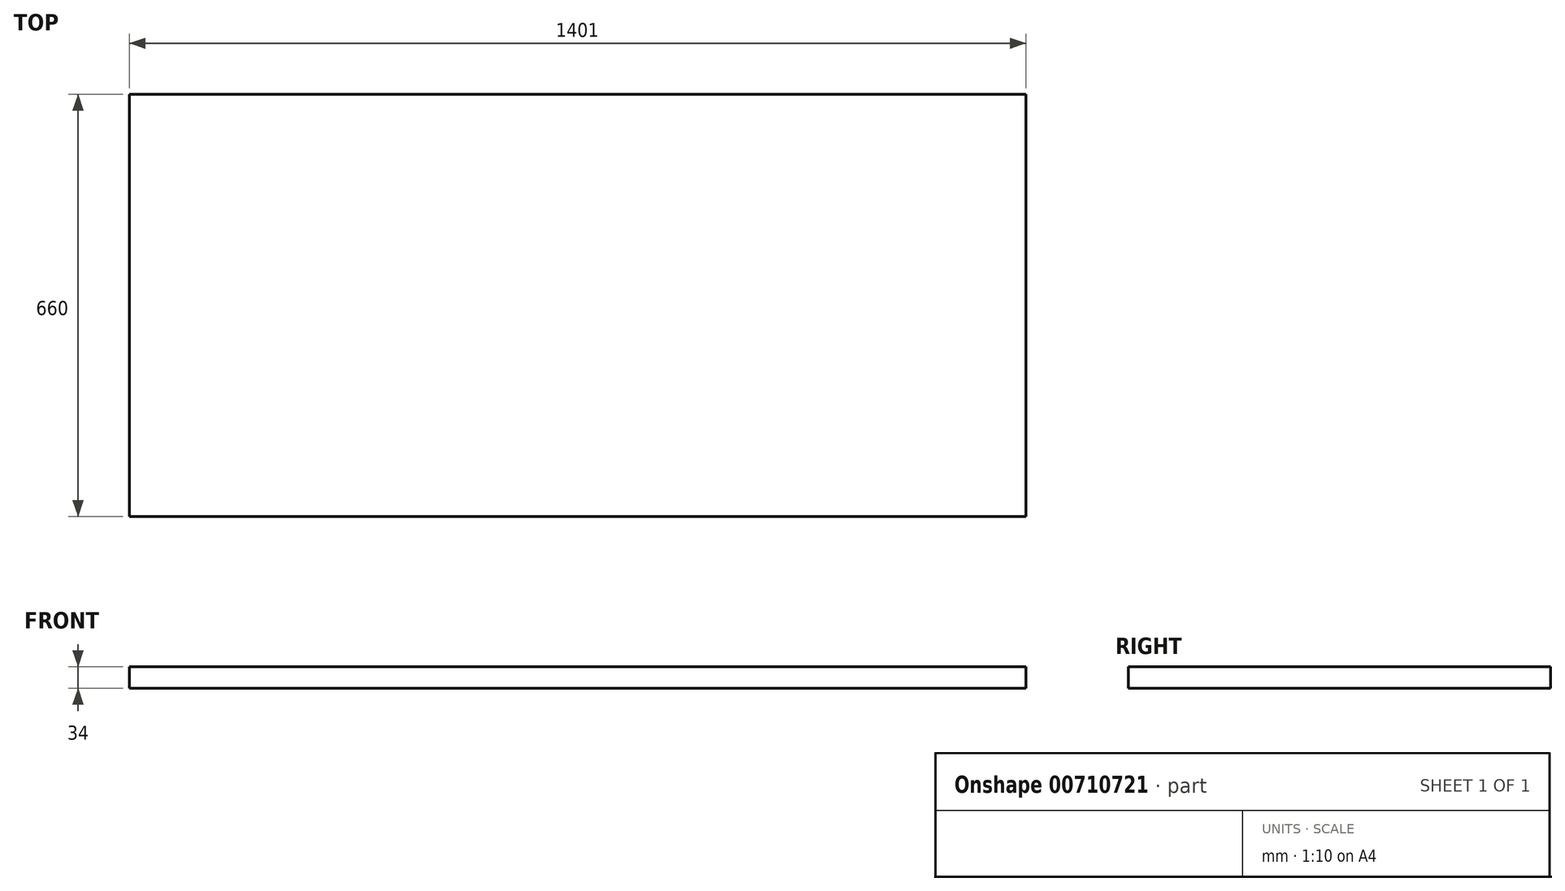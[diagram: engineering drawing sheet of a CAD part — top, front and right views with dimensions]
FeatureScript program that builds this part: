
annotation { "Feature Type Name" : "Feature", "Feature Type Description" : "" }
export const myFeature = defineFeature(function(context is Context, id is Id, definition is map)
    precondition{}
    {
        {
            var Q0;
            Q0=qCreatedBy(makeId("Top.planeOp"),FACE);
            var sketch = newSketch(context, id + "F0", { "sketchPlane" : qUnion([Q0])});
            skLineSegment(sketch, "E0", {"start": v(0, 0) * mm, "end": v(0, 660) * mm});
            skLineSegment(sketch, "E1", {"start": v(0, 660) * mm, "end": v(-1401, 660) * mm});
            skLineSegment(sketch, "E2", {"start": v(-1401, 660) * mm, "end": v(-1401, 0) * mm});
            skLineSegment(sketch, "E3", {"start": v(-1401, 0) * mm, "end": v(0, 0) * mm});
            skSolve(sketch);
        }
        {
            var Q0;
            Q0 = qSketchRegion(id + "F0", true);
            extrude(context, id + "F1", {"entities" : qUnion([Q0]), "depth" : 34 * mm, "offsetDistance" : 25 * mm});
        }
    });
